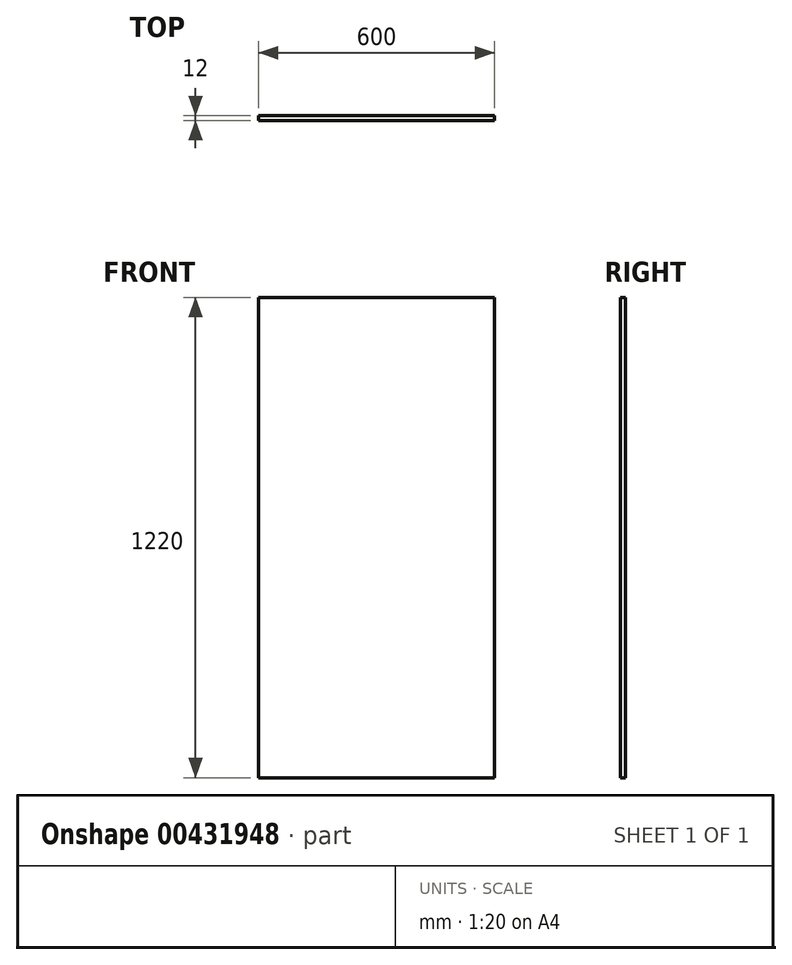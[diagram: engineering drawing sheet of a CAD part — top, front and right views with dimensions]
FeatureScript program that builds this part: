
annotation { "Feature Type Name" : "Feature", "Feature Type Description" : "" }
export const myFeature = defineFeature(function(context is Context, id is Id, definition is map)
    precondition{}
    {
        {
            var Q0;
            Q0=qCreatedBy(makeId("Front.planeOp"),FACE);
            var sketch = newSketch(context, id + "F0", { "sketchPlane" : qUnion([Q0])});
            skLineSegment(sketch, "E0.bottom", {"start": v(0, 0) * mm, "end": v(-600, 0) * mm});
            skLineSegment(sketch, "E0.top", {"start": v(0, 1220) * mm, "end": v(-600, 1220) * mm});
            skLineSegment(sketch, "E0.left", {"start": v(0, 0) * mm, "end": v(0, 1220) * mm});
            skLineSegment(sketch, "E0.right", {"start": v(-600, 0) * mm, "end": v(-600, 1220) * mm});
            skSolve(sketch);
        }
        {
            var Q0;
            Q0 = qSketchRegion(id + "F0", true);
            extrude(context, id + "F1", {"entities" : qUnion([Q0]), "depth" : 12 * mm, "offsetDistance" : 25 * mm});
        }
    });
